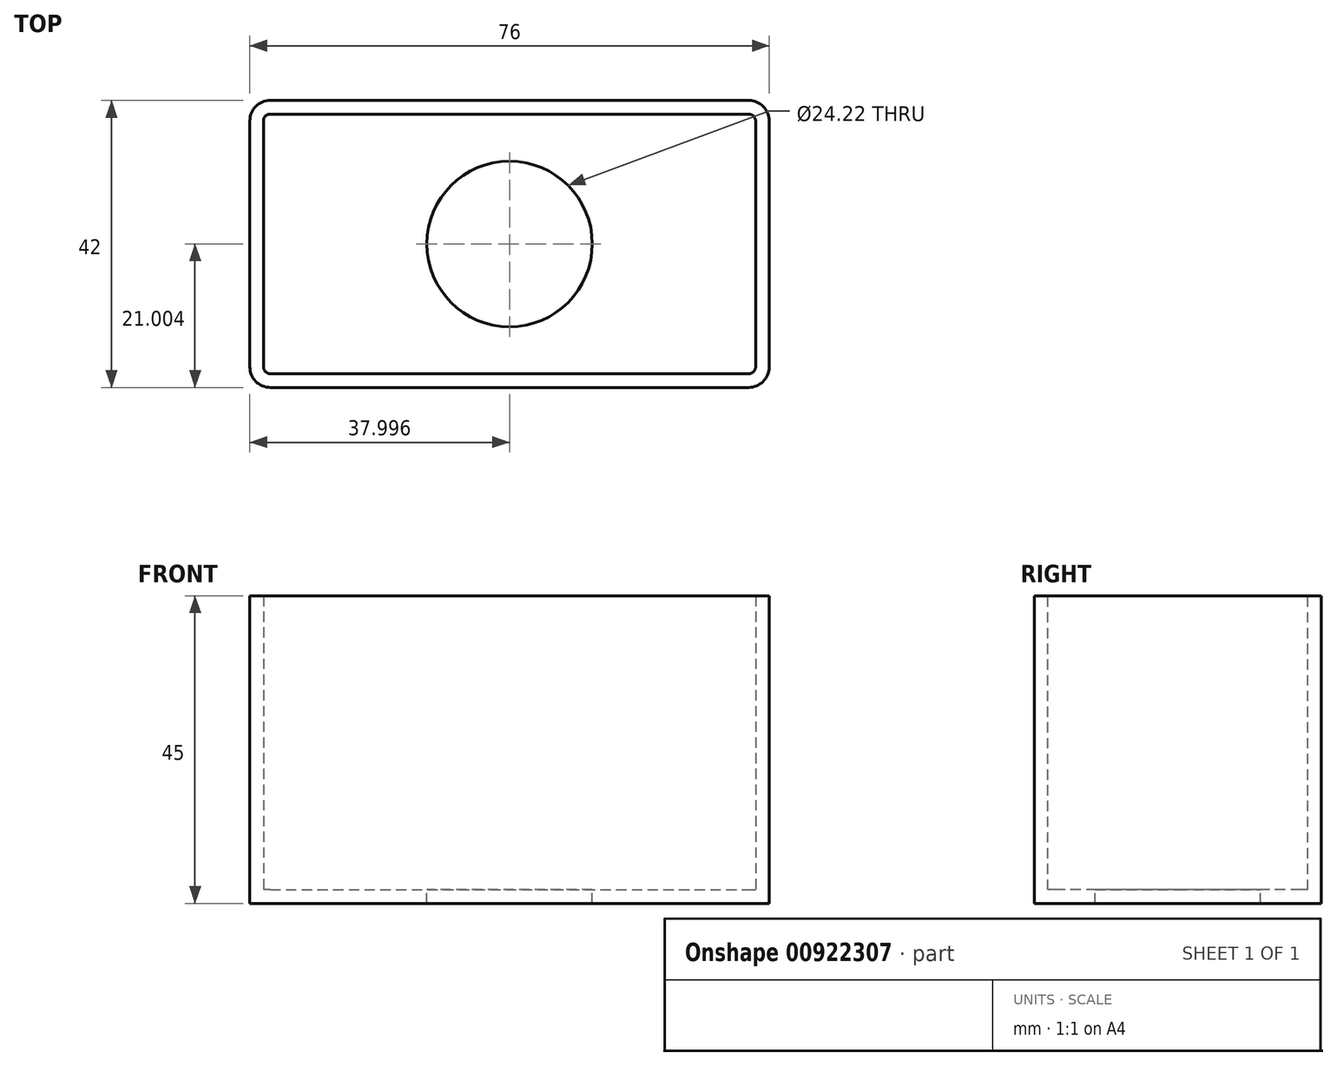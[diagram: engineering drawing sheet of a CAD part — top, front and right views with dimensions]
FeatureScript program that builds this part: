
annotation { "Feature Type Name" : "Feature", "Feature Type Description" : "" }
export const myFeature = defineFeature(function(context is Context, id is Id, definition is map)
    precondition{}
    {
        {
            var Q0;
            Q0=qCreatedBy(makeId("Top.planeOp"),FACE);
            var sketch = newSketch(context, id + "F0", { "sketchPlane" : qUnion([Q0])});
            skLineSegment(sketch, "E0.bottom", {"start": v(-30.4, 18.82) * mm, "end": v(45.6, 18.82) * mm});
            skLineSegment(sketch, "E0.top", {"start": v(-30.4, -23.18) * mm, "end": v(45.6, -23.18) * mm});
            skLineSegment(sketch, "E0.left", {"start": v(-30.4, 18.82) * mm, "end": v(-30.4, -23.18) * mm});
            skLineSegment(sketch, "E0.right", {"start": v(45.6, 18.82) * mm, "end": v(45.6, -23.18) * mm});
            skSolve(sketch);
        }
        {
            var Q0;
            Q0=makeQuery(id+"F0.imprint","IMPRINT",FACE,{"disambiguationData":[TD([[makeQuery(id+"F0.imprint","IMPRINT",EDGE,{"derivedFrom":sQuery(id+"F0.wireOp",EDGE,"E0.bottom")}),-1.0]])]});
            extrude(context, id + "F1", {"entities" : qUnion([Q0]), "depth" : 45 * mm, "offsetDistance" : 25 * mm});
        }
        {
            var Q0;
            Q0=makeQuery(id+"F1.opExtrude","SWEPT_EDGE",EDGE,{"disambiguationData":[OSD([sQuery(id+"F0.wireOp",EDGE,"E0.top"),sQuery(id+"F0.wireOp",EDGE,"E0.left")])]});
            var Q1;
            Q1=makeQuery(id+"F1.opExtrude","SWEPT_EDGE",EDGE,{"disambiguationData":[OSD([sQuery(id+"F0.wireOp",EDGE,"E0.bottom"),sQuery(id+"F0.wireOp",EDGE,"E0.left")])]});
            var Q2;
            Q2=makeQuery(id+"F1.opExtrude","SWEPT_EDGE",EDGE,{"disambiguationData":[OSD([sQuery(id+"F0.wireOp",EDGE,"E0.top"),sQuery(id+"F0.wireOp",EDGE,"E0.right")])]});
            var Q3;
            Q3=makeQuery(id+"F1.opExtrude","SWEPT_EDGE",EDGE,{"disambiguationData":[OSD([sQuery(id+"F0.wireOp",EDGE,"E0.bottom"),sQuery(id+"F0.wireOp",EDGE,"E0.right")])]});
            fillet(context, id + "F2", {"entities" : qUnion([Q0, Q1, Q2, Q3]), "radius" : 3 * mm, "tangentPropagation" : true, "allowEdgeOverflow" : false});
        }
        {
            var Q0;
            Q0=makeQuery(id+"F1.opExtrude","CAP_FACE",FACE,{"disambiguationData":[OSD([sQuery(id+"F0.wireOp",EDGE,"E0.bottom"),sQuery(id+"F0.wireOp",EDGE,"E0.top"),sQuery(id+"F0.wireOp",EDGE,"E0.left"),sQuery(id+"F0.wireOp",EDGE,"E0.right")])],"isStart":false});
            shell(context, id + "F3", {"entities" : qUnion([Q0]), "thickness" : 2 * mm});
        }
        {
            var Q0;
            Q0=makeQuery(id+"F3.opShell","OFFSET_FACE",FACE,{"disambiguationData":[OSD([sQuery(id+"F0.wireOp",EDGE,"E0.bottom"),sQuery(id+"F0.wireOp",EDGE,"E0.top"),sQuery(id+"F0.wireOp",EDGE,"E0.left"),sQuery(id+"F0.wireOp",EDGE,"E0.right")])]});
            var sketch = newSketch(context, id + "F4", { "sketchPlane" : qUnion([Q0])});
            skCircle(sketch, "E1", {"center": v(7.6, -2.18) * mm, "radius": 12.11 * mm});
            skPoint(sketch, "E1.centerSnap0", {"position": v(43.6, -2.18) * mm});
            skPoint(sketch, "E1.centerSnap1", {"position": v(7.6, 16.82) * mm});
            skSolve(sketch);
        }
        {
            var Q0;
            Q0=makeQuery(id+"F4.imprint","IMPRINT",FACE,{"disambiguationData":[TD([[makeQuery(id+"F4.imprint","IMPRINT",EDGE,{"derivedFrom":sQuery(id+"F4.wireOp",EDGE,"E1")}),1.0]])]});
            extrude(context, id + "F5", {"entities" : qUnion([Q0]), "operationType" : NewBodyOperationType.REMOVE, "oppositeDirection" : true, "depth" : 25 * mm, "offsetDistance" : 25 * mm});
        }
    });
